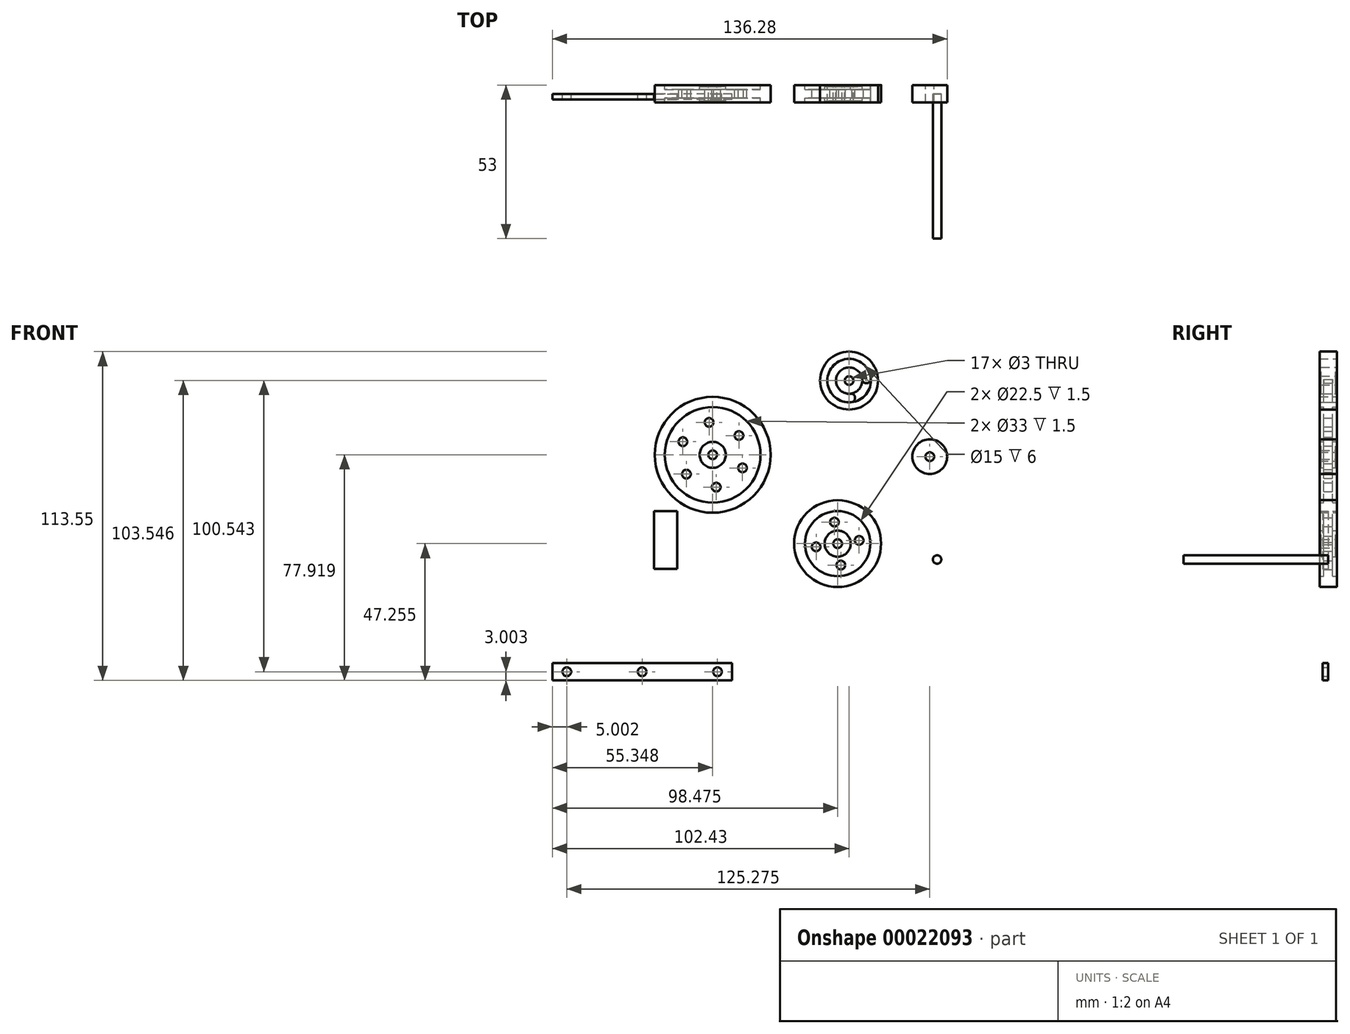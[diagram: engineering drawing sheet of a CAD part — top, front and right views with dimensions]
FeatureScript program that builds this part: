
annotation { "Feature Type Name" : "Feature", "Feature Type Description" : "" }
export const myFeature = defineFeature(function(context is Context, id is Id, definition is map)
    precondition{}
    {
        {
            var Q0;
            Q0=qCreatedBy(makeId("Front.planeOp"),FACE);
            var sketch = newSketch(context, id + "F0", { "sketchPlane" : qUnion([Q0])});
            skCircle(sketch, "E0", {"center": v(-47.08, 9.09) * mm, "radius": 20 * mm});
            skCircle(sketch, "E1", {"center": v(0, 34.72) * mm, "radius": 10 * mm});
            skCircle(sketch, "E2", {"center": v(-3.96, -21.57) * mm, "radius": 15 * mm});
            skCircle(sketch, "E3", {"center": v(27.85, 8.45) * mm, "radius": 6 * mm});
            skCircle(sketch, "E4", {"center": v(-47.08, 9.09) * mm, "radius": 1.5 * mm});
            skCircle(sketch, "E5", {"center": v(0, 34.72) * mm, "radius": 1.5 * mm});
            skCircle(sketch, "E6", {"center": v(27.85, 8.45) * mm, "radius": 1.5 * mm});
            skCircle(sketch, "E7", {"center": v(-3.96, -21.57) * mm, "radius": 1.5 * mm});
            skArc(sketch, "E8", {"start": v(-1.02, 42.15) * mm, "mid": v(-0.43, 39.22) * mm, "end": v(-0.4, 42.2) * mm});
            skArc(sketch, "E9.1.0", {"start": v(-7.43, 33.7) * mm, "mid": v(-4.5, 34.29) * mm, "end": v(-7.49, 34.32) * mm});
            skArc(sketch, "E9.2.0", {"start": v(1.02, 27.29) * mm, "mid": v(0.43, 30.2) * mm, "end": v(0.4, 27.23) * mm});
            skArc(sketch, "E9.3.0", {"start": v(7.43, 35.73) * mm, "mid": v(4.5, 35.14) * mm, "end": v(7.49, 35.1) * mm});
            skCircle(sketch, "E10", {"center": v(0, 34.72) * mm, "radius": 7.5 * mm});
            skPoint(sketch, "E11", {"position": v(0.4, 27.23) * mm});
            skPoint(sketch, "E12", {"position": v(1.02, 27.29) * mm});
            skCircle(sketch, "E13", {"center": v(0, 34.72) * mm, "radius": 4.53 * mm});
            skCircle(sketch, "E14", {"center": v(-5.07, -14.16) * mm, "radius": 1.5 * mm});
            skCircle(sketch, "E15.1.0", {"center": v(-11.37, -22.7) * mm, "radius": 1.5 * mm});
            skCircle(sketch, "E15.2.0", {"center": v(-2.84, -29) * mm, "radius": 1.5 * mm});
            skCircle(sketch, "E15.3.0", {"center": v(3.46, -20.46) * mm, "radius": 1.5 * mm});
            skCircle(sketch, "E16", {"center": v(-3.96, -21.57) * mm, "radius": 4.5 * mm});
            skCircle(sketch, "E17", {"center": v(-3.96, -21.57) * mm, "radius": 11.25 * mm});
            skCircle(sketch, "E18", {"center": v(-47.08, 9.09) * mm, "radius": 4.5 * mm});
            skCircle(sketch, "E19", {"center": v(-48.3, 20.27) * mm, "radius": 1.5 * mm});
            skCircle(sketch, "E20.1.0", {"center": v(-57.38, 13.62) * mm, "radius": 1.5 * mm});
            skCircle(sketch, "E20.2.0", {"center": v(-56.15, 2.43) * mm, "radius": 1.5 * mm});
            skCircle(sketch, "E20.3.0", {"center": v(-45.86, -2.1) * mm, "radius": 1.5 * mm});
            skCircle(sketch, "E20.4.0", {"center": v(-36.78, 4.56) * mm, "radius": 1.5 * mm});
            skCircle(sketch, "E20.5.0", {"center": v(-38.01, 15.74) * mm, "radius": 1.5 * mm});
            skCircle(sketch, "E21", {"center": v(-47.08, 9.09) * mm, "radius": 16.5 * mm});
            skCircle(sketch, "E22", {"center": v(30.36, -27.06) * mm, "radius": 1.45 * mm});
            skLineSegment(sketch, "E23.bottom", {"start": v(-40.43, -62.83) * mm, "end": v(-102.43, -62.83) * mm});
            skLineSegment(sketch, "E23.top", {"start": v(-40.43, -68.83) * mm, "end": v(-102.43, -68.83) * mm});
            skLineSegment(sketch, "E23.left", {"start": v(-40.43, -62.83) * mm, "end": v(-40.43, -68.83) * mm});
            skLineSegment(sketch, "E23.right", {"start": v(-102.43, -62.83) * mm, "end": v(-102.43, -68.83) * mm});
            skCircle(sketch, "E24", {"center": v(-97.43, -65.83) * mm, "radius": 1.5 * mm});
            skLineSegment(sketch, "E25", {"start": v(-98.93, -65.83) * mm, "end": v(-40.43, -65.83) * mm});
            skCircle(sketch, "E26", {"center": v(-45.43, -65.83) * mm, "radius": 1.5 * mm});
            skCircle(sketch, "E27", {"center": v(-71.43, -65.83) * mm, "radius": 1.5 * mm});
            skPoint(sketch, "E28.orphan", {"position": v(-102.43, -65.83) * mm});
            skLineSegment(sketch, "E29.bottom", {"start": v(-67.39, -10.36) * mm, "end": v(-59.39, -10.36) * mm});
            skLineSegment(sketch, "E29.top", {"start": v(-67.39, -30.36) * mm, "end": v(-59.39, -30.36) * mm});
            skLineSegment(sketch, "E29.left", {"start": v(-67.39, -10.36) * mm, "end": v(-67.39, -30.36) * mm});
            skLineSegment(sketch, "E29.right", {"start": v(-59.39, -10.36) * mm, "end": v(-59.39, -30.36) * mm});
            skLineSegment(sketch, "E30", {"start": v(-63.39, -10.36) * mm, "end": v(-63.39, -28.38) * mm});
            skSolve(sketch);
        }
        {
            var Q0;
            Q0=makeQuery(id+"F0.imprint","IMPRINT",FACE,{"disambiguationData":[TD([[makeQuery(id+"F0.imprint","IMPRINT",EDGE,{"derivedFrom":sQuery(id+"F0.wireOp",EDGE,"E1")}),1.0]])]});
            extrude(context, id + "F1", {"entities" : qUnion([Q0]), "endBound" : BoundingType.SYMMETRIC, "depth" : 6 * mm});
        }
        {
            var Q0;
            {var subQ3=sQuery(id+"F0.wireOp",EDGE,"E8");var subQ5=sQuery(id+"F0.wireOp",EDGE,"E10");var subQ7=makeQuery(id+"F0.imprint","INTERSECT",VERTEX,{"disambiguationData":[OD(1.0)],"derivedFrom":[subQ3,subQ5]});Q0=makeQuery(id+"F0.imprint","IMPRINT",FACE,{"disambiguationData":[TD([[makeQuery(id+"F0.imprint","IMPRINT",EDGE,{"disambiguationData":[TD([[subQ7,1.0]])],"derivedFrom":subQ3}),-1.0]])]});}
            var Q1;
            {var subQ3=sQuery(id+"F0.wireOp",EDGE,"E8");var subQ5=sQuery(id+"F0.wireOp",EDGE,"E10");var subQ7=makeQuery(id+"F0.imprint","INTERSECT",VERTEX,{"disambiguationData":[OD(0.0)],"derivedFrom":[subQ3,subQ5]});Q1=makeQuery(id+"F0.imprint","IMPRINT",FACE,{"disambiguationData":[TD([[makeQuery(id+"F0.imprint","IMPRINT",EDGE,{"disambiguationData":[TD([[subQ7,-1.0]])],"derivedFrom":subQ3}),-1.0]])]});}
            var Q2;
            {var subQ3=sQuery(id+"F0.wireOp",EDGE,"E9.1.0");var subQ5=sQuery(id+"F0.wireOp",EDGE,"E10");var subQ7=makeQuery(id+"F0.imprint","INTERSECT",VERTEX,{"disambiguationData":[OD(0.0)],"derivedFrom":[subQ3,subQ5]});Q2=makeQuery(id+"F0.imprint","IMPRINT",FACE,{"disambiguationData":[TD([[makeQuery(id+"F0.imprint","IMPRINT",EDGE,{"disambiguationData":[TD([[subQ7,-1.0]])],"derivedFrom":subQ3}),-1.0]])]});}
            var Q3;
            {var subQ3=sQuery(id+"F0.wireOp",EDGE,"E9.2.0");var subQ5=sQuery(id+"F0.wireOp",EDGE,"E10");var subQ7=makeQuery(id+"F0.imprint","INTERSECT",VERTEX,{"disambiguationData":[OD(0.0)],"derivedFrom":[subQ3,subQ5]});Q3=makeQuery(id+"F0.imprint","IMPRINT",FACE,{"disambiguationData":[TD([[makeQuery(id+"F0.imprint","IMPRINT",EDGE,{"disambiguationData":[TD([[subQ7,-1.0]])],"derivedFrom":subQ3}),-1.0]])]});}
            extrude(context, id + "F2", {"entities" : qUnion([Q0, Q1, Q2, Q3]), "endBound" : BoundingType.SYMMETRIC, "depth" : 3 * mm});
        }
        {
            var Q0;
            Q0=makeQuery(id+"F0.imprint","IMPRINT",FACE,{"disambiguationData":[TD([[makeQuery(id+"F0.imprint","IMPRINT",EDGE,{"derivedFrom":sQuery(id+"F0.wireOp",EDGE,"E5")}),-1.0]])]});
            extrude(context, id + "F3", {"entities" : qUnion([Q0]), "operationType" : NewBodyOperationType.ADD, "endBound" : BoundingType.SYMMETRIC, "depth" : 5 * mm});
        }
        {
            var Q0;
            Q0=makeQuery(id+"F0.imprint","IMPRINT",FACE,{"disambiguationData":[TD([[makeQuery(id+"F0.imprint","IMPRINT",EDGE,{"derivedFrom":sQuery(id+"F0.wireOp",EDGE,"E3")}),1.0]])]});
            extrude(context, id + "F4", {"entities" : qUnion([Q0]), "endBound" : BoundingType.SYMMETRIC, "depth" : 6 * mm});
        }
        {
            var Q0;
            Q0=makeQuery(id+"F0.imprint","IMPRINT",FACE,{"disambiguationData":[TD([[makeQuery(id+"F0.imprint","IMPRINT",EDGE,{"derivedFrom":sQuery(id+"F0.wireOp",EDGE,"E7")}),-1.0]])]});
            extrude(context, id + "F5", {"entities" : qUnion([Q0]), "endBound" : BoundingType.SYMMETRIC, "depth" : 5 * mm});
        }
        {
            var Q0;
            Q0=makeQuery(id+"F0.imprint","IMPRINT",FACE,{"disambiguationData":[TD([[makeQuery(id+"F0.imprint","IMPRINT",EDGE,{"derivedFrom":sQuery(id+"F0.wireOp",EDGE,"E14")}),-1.0]])]});
            extrude(context, id + "F6", {"entities" : qUnion([Q0]), "operationType" : NewBodyOperationType.ADD, "endBound" : BoundingType.SYMMETRIC, "depth" : 3 * mm});
        }
        {
            var Q0;
            Q0=makeQuery(id+"F0.imprint","IMPRINT",FACE,{"disambiguationData":[TD([[makeQuery(id+"F0.imprint","IMPRINT",EDGE,{"derivedFrom":sQuery(id+"F0.wireOp",EDGE,"E2")}),1.0]])]});
            extrude(context, id + "F7", {"entities" : qUnion([Q0]), "operationType" : NewBodyOperationType.ADD, "endBound" : BoundingType.SYMMETRIC, "depth" : 6 * mm});
        }
        {
            var Q0;
            Q0=makeQuery(id+"F0.imprint","IMPRINT",FACE,{"disambiguationData":[TD([[makeQuery(id+"F0.imprint","IMPRINT",EDGE,{"derivedFrom":sQuery(id+"F0.wireOp",EDGE,"E4")}),-1.0]])]});
            extrude(context, id + "F8", {"entities" : qUnion([Q0]), "endBound" : BoundingType.SYMMETRIC, "depth" : 5 * mm});
        }
        {
            var Q0;
            Q0=makeQuery(id+"F0.imprint","IMPRINT",FACE,{"disambiguationData":[TD([[makeQuery(id+"F0.imprint","IMPRINT",EDGE,{"derivedFrom":sQuery(id+"F0.wireOp",EDGE,"E18")}),-1.0]])]});
            extrude(context, id + "F9", {"entities" : qUnion([Q0]), "operationType" : NewBodyOperationType.ADD, "endBound" : BoundingType.SYMMETRIC, "depth" : 3 * mm});
        }
        {
            var Q0;
            Q0=makeQuery(id+"F0.imprint","IMPRINT",FACE,{"disambiguationData":[TD([[makeQuery(id+"F0.imprint","IMPRINT",EDGE,{"derivedFrom":sQuery(id+"F0.wireOp",EDGE,"E0")}),1.0]])]});
            extrude(context, id + "F10", {"entities" : qUnion([Q0]), "operationType" : NewBodyOperationType.ADD, "endBound" : BoundingType.SYMMETRIC, "depth" : 6 * mm});
        }
        {
            var Q0;
            Q0=makeQuery(id+"F0.imprint","IMPRINT",FACE,{"disambiguationData":[TD([[makeQuery(id+"F0.imprint","IMPRINT",EDGE,{"derivedFrom":sQuery(id+"F0.wireOp",EDGE,"E22")}),1.0]])]});
            extrude(context, id + "F11", {"entities" : qUnion([Q0]), "depth" : 50 * mm});
        }
        {
            var Q0;
            {var subQ13=sQuery(id+"F0.wireOp",EDGE,"E23.bottom");Q0=makeQuery(id+"F0.imprint","IMPRINT",FACE,{"disambiguationData":[TD([[makeQuery(id+"F0.imprint","IMPRINT",EDGE,{"derivedFrom":subQ13}),1.0]])]});}
            extrude(context, id + "F12", {"entities" : qUnion([Q0]), "depth" : 2 * mm});
        }
        {
            var Q0;
            Q0=makeQuery(id+"F0.imprint","IMPRINT",FACE,{"disambiguationData":[TD([[makeQuery(id+"F0.imprint","IMPRINT",EDGE,{"derivedFrom":sQuery(id+"F0.wireOp",EDGE,"E29.top")}),1.0]])]});
            extrude(context, id + "F13", {"entities" : qUnion([Q0]), "depth" : 2 * mm});
        }
    });
